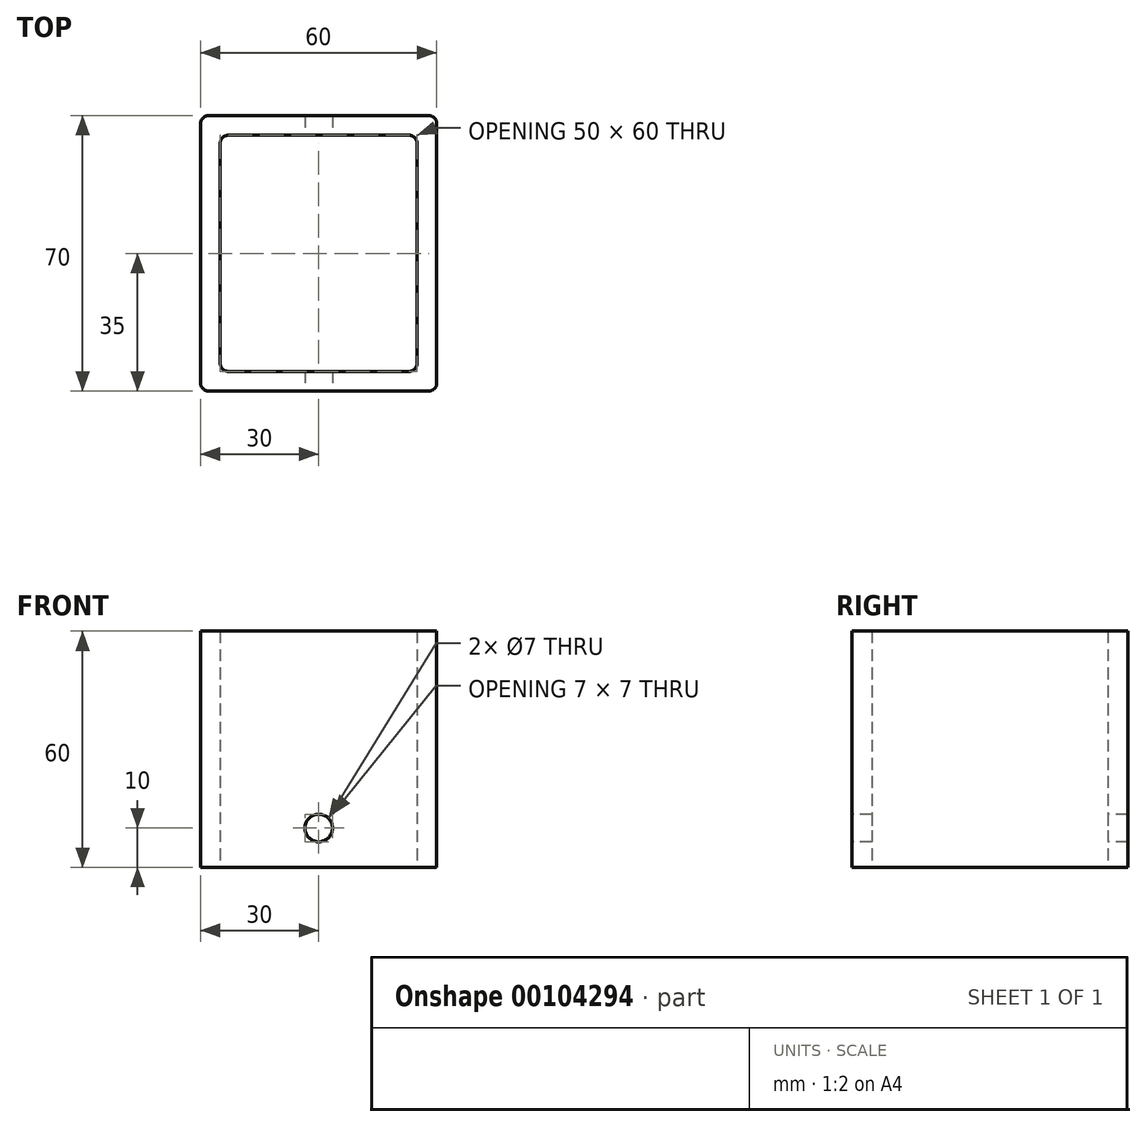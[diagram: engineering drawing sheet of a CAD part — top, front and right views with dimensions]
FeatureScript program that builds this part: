
annotation { "Feature Type Name" : "Feature", "Feature Type Description" : "" }
export const myFeature = defineFeature(function(context is Context, id is Id, definition is map)
    precondition{}
    {
        {
            var Q0;
            Q0=qCreatedBy(makeId("Top.planeOp"),FACE);
            var sketch = newSketch(context, id + "F0", { "sketchPlane" : qUnion([Q0])});
            skLineSegment(sketch, "E0.bottom", {"start": v(-30, 35) * mm, "end": v(30, 35) * mm});
            skLineSegment(sketch, "E0.top", {"start": v(-30, -35) * mm, "end": v(30, -35) * mm});
            skLineSegment(sketch, "E0.left", {"start": v(-30, 35) * mm, "end": v(-30, -35) * mm});
            skLineSegment(sketch, "E0.right", {"start": v(30, 35) * mm, "end": v(30, -35) * mm});
            skPoint(sketch, "E0.middle", {"position": v(0, 0) * mm});
            skLineSegment(sketch, "E1.bottom", {"start": v(-25, 30) * mm, "end": v(25, 30) * mm});
            skLineSegment(sketch, "E1.top", {"start": v(-25, -30) * mm, "end": v(25, -30) * mm});
            skLineSegment(sketch, "E1.left", {"start": v(-25, 30) * mm, "end": v(-25, -30) * mm});
            skLineSegment(sketch, "E1.right", {"start": v(25, 30) * mm, "end": v(25, -30) * mm});
            skSolve(sketch);
        }
        {
            var Q0;
            Q0=makeQuery(id+"F0.imprint","IMPRINT",FACE,{"disambiguationData":[TD([[makeQuery(id+"F0.imprint","IMPRINT",EDGE,{"derivedFrom":sQuery(id+"F0.wireOp",EDGE,"E0.bottom")}),-1.0]])]});
            extrude(context, id + "F1", {"entities" : qUnion([Q0]), "depth" : 60 * mm});
        }
        {
            var Q0;
            Q0=makeQuery(id+"F1.opExtrude","SWEPT_EDGE",EDGE,{"disambiguationData":[OSD([sQuery(id+"F0.wireOp",EDGE,"E0.top"),sQuery(id+"F0.wireOp",EDGE,"E0.left")])]});
            var Q1;
            Q1=makeQuery(id+"F1.opExtrude","SWEPT_EDGE",EDGE,{"disambiguationData":[OSD([sQuery(id+"F0.wireOp",EDGE,"E0.top"),sQuery(id+"F0.wireOp",EDGE,"E0.right")])]});
            var Q2;
            Q2=makeQuery(id+"F1.opExtrude","SWEPT_EDGE",EDGE,{"disambiguationData":[OSD([sQuery(id+"F0.wireOp",EDGE,"E0.bottom"),sQuery(id+"F0.wireOp",EDGE,"E0.left")])]});
            var Q3;
            Q3=makeQuery(id+"F1.opExtrude","SWEPT_EDGE",EDGE,{"disambiguationData":[OSD([sQuery(id+"F0.wireOp",EDGE,"E0.bottom"),sQuery(id+"F0.wireOp",EDGE,"E0.right")])]});
            var Q4;
            Q4=makeQuery(id+"F1.opExtrude","SWEPT_EDGE",EDGE,{"disambiguationData":[OSD([sQuery(id+"F0.wireOp",EDGE,"E1.top"),sQuery(id+"F0.wireOp",EDGE,"E1.right")])]});
            var Q5;
            Q5=makeQuery(id+"F1.opExtrude","SWEPT_EDGE",EDGE,{"disambiguationData":[OSD([sQuery(id+"F0.wireOp",EDGE,"E1.bottom"),sQuery(id+"F0.wireOp",EDGE,"E1.left")])]});
            var Q6;
            Q6=makeQuery(id+"F1.opExtrude","SWEPT_EDGE",EDGE,{"disambiguationData":[OSD([sQuery(id+"F0.wireOp",EDGE,"E1.bottom"),sQuery(id+"F0.wireOp",EDGE,"E1.right")])]});
            var Q7;
            Q7=makeQuery(id+"F1.opExtrude","SWEPT_EDGE",EDGE,{"disambiguationData":[OSD([sQuery(id+"F0.wireOp",EDGE,"E1.top"),sQuery(id+"F0.wireOp",EDGE,"E1.left")])]});
            fillet(context, id + "F2", {"entities" : qUnion([Q0, Q1, Q2, Q3, Q4, Q5, Q6, Q7]), "radius" : 2 * mm, "tangentPropagation" : true, "allowEdgeOverflow" : false});
        }
        {
            var Q0;
            Q0=qCreatedBy(makeId("Front.planeOp"),FACE);
            var sketch = newSketch(context, id + "F3", { "sketchPlane" : qUnion([Q0])});
            skCircle(sketch, "E2", {"center": v(0, 10) * mm, "radius": 3.5 * mm});
            skSolve(sketch);
        }
        {
            var Q0;
            Q0 = qSketchRegion(id + "F3", true);
            extrude(context, id + "F4", {"entities" : qUnion([Q0]), "operationType" : NewBodyOperationType.REMOVE, "endBound" : BoundingType.SYMMETRIC, "oppositeDirection" : true, "depth" : 70 * mm});
        }
    });
